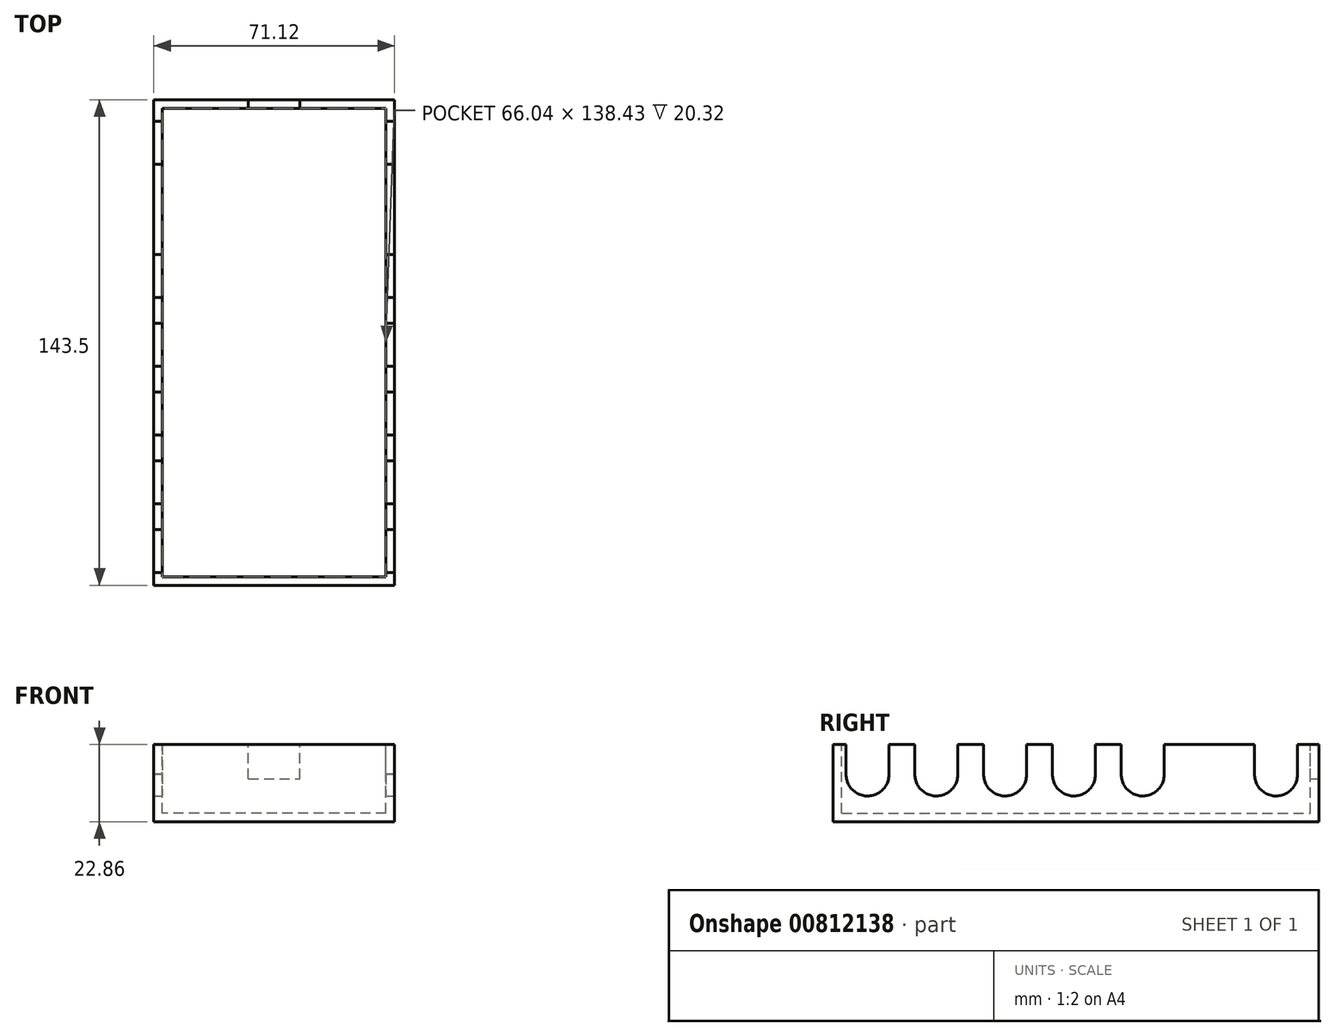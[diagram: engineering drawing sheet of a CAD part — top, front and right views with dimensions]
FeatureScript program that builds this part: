
annotation { "Feature Type Name" : "Feature", "Feature Type Description" : "" }
export const myFeature = defineFeature(function(context is Context, id is Id, definition is map)
    precondition{}
    {
        {
            var Q0;
            Q0=qCreatedBy(makeId("Top.planeOp"),FACE);
            var sketch = newSketch(context, id + "F0", { "sketchPlane" : qUnion([Q0])});
            skLineSegment(sketch, "E0.bottom", {"start": v(-35.56, -71.76) * mm, "end": v(35.56, -71.76) * mm});
            skLineSegment(sketch, "E0.top", {"start": v(-35.56, 71.76) * mm, "end": v(35.56, 71.76) * mm});
            skLineSegment(sketch, "E0.left", {"start": v(-35.56, -71.76) * mm, "end": v(-35.56, 71.76) * mm});
            skLineSegment(sketch, "E0.right", {"start": v(35.56, -71.76) * mm, "end": v(35.56, 71.76) * mm});
            skPoint(sketch, "E0.middle", {"position": v(0, 0) * mm});
            skSolve(sketch);
        }
        {
            var Q0;
            Q0 = qSketchRegion(id + "F0", true);
            extrude(context, id + "F1", {"entities" : qUnion([Q0]), "depth" : 22.86 * mm, "offsetDistance" : 25.4 * mm});
        }
        {
            var Q0;
            Q0=makeQuery(id+"F1.opExtrude","CAP_FACE",FACE,{"disambiguationData":[OSD([sQuery(id+"F0.wireOp",EDGE,"E0.bottom"),sQuery(id+"F0.wireOp",EDGE,"E0.top"),sQuery(id+"F0.wireOp",EDGE,"E0.left"),sQuery(id+"F0.wireOp",EDGE,"E0.right")])],"isStart":false});
            var sketch = newSketch(context, id + "F2", { "sketchPlane" : qUnion([Q0])});
            skLineSegment(sketch, "E1.0", {"start": v(33.02, 69.22) * mm, "end": v(-33.02, 69.22) * mm});
            skLineSegment(sketch, "E1.1", {"start": v(33.02, -69.22) * mm, "end": v(33.02, 69.22) * mm});
            skLineSegment(sketch, "E1.2", {"start": v(-33.02, -69.22) * mm, "end": v(33.02, -69.22) * mm});
            skLineSegment(sketch, "E1.3", {"start": v(-33.02, 69.22) * mm, "end": v(-33.02, -69.22) * mm});
            skSolve(sketch);
        }
        {
            var Q0;
            Q0 = qSketchRegion(id + "F2", true);
            extrude(context, id + "F3", {"entities" : qUnion([Q0]), "operationType" : NewBodyOperationType.REMOVE, "oppositeDirection" : true, "depth" : 20.32 * mm, "offsetDistance" : 25.4 * mm});
        }
        {
            var Q0;
            Q0=makeQuery(id+"F1.opExtrude","SWEPT_FACE",FACE,{"disambiguationData":[OSD([sQuery(id+"F0.wireOp",EDGE,"E0.right")])]});
            var sketch = newSketch(context, id + "F4", { "sketchPlane" : qUnion([Q0])});
            skArc(sketch, "E2", {"start": v(-67.94, 14.06) * mm, "mid": v(-61.54, 7.62) * mm, "end": v(-55.25, 14.18) * mm});
            skLineSegment(sketch, "E3", {"start": v(-67.94, 14.06) * mm, "end": v(-67.94, 22.86) * mm});
            skLineSegment(sketch, "E4", {"start": v(-55.25, 13.76) * mm, "end": v(-55.25, 22.86) * mm});
            skLineSegment(sketch, "E5", {"start": v(-55.25, 22.86) * mm, "end": v(-67.94, 22.86) * mm});
            skLineSegment(sketch, "E6.1.0.0", {"start": v(-34.93, 22.86) * mm, "end": v(-47.62, 22.86) * mm});
            skLineSegment(sketch, "E6.1.0.1", {"start": v(-34.93, 13.76) * mm, "end": v(-34.93, 22.86) * mm});
            skLineSegment(sketch, "E6.1.0.2", {"start": v(-47.62, 14.06) * mm, "end": v(-47.62, 22.86) * mm});
            skArc(sketch, "E6.1.0.3", {"start": v(-47.62, 14.06) * mm, "mid": v(-41.22, 7.62) * mm, "end": v(-34.93, 14.18) * mm});
            skLineSegment(sketch, "E6.2.0.0", {"start": v(-14.6, 22.86) * mm, "end": v(-27.3, 22.86) * mm});
            skLineSegment(sketch, "E6.2.0.1", {"start": v(-14.6, 13.76) * mm, "end": v(-14.6, 22.86) * mm});
            skLineSegment(sketch, "E6.2.0.2", {"start": v(-27.3, 14.06) * mm, "end": v(-27.3, 22.86) * mm});
            skArc(sketch, "E6.2.0.3", {"start": v(-27.3, 14.06) * mm, "mid": v(-20.9, 7.62) * mm, "end": v(-14.6, 14.18) * mm});
            skLineSegment(sketch, "E6.3.0.0", {"start": v(5.71, 22.86) * mm, "end": v(-6.98, 22.86) * mm});
            skLineSegment(sketch, "E6.3.0.1", {"start": v(5.71, 13.76) * mm, "end": v(5.71, 22.86) * mm});
            skLineSegment(sketch, "E6.3.0.2", {"start": v(-6.98, 14.06) * mm, "end": v(-6.98, 22.86) * mm});
            skArc(sketch, "E6.3.0.3", {"start": v(-6.98, 14.06) * mm, "mid": v(-0.58, 7.62) * mm, "end": v(5.71, 14.18) * mm});
            skLineSegment(sketch, "E6.4.0.0", {"start": v(26.03, 22.86) * mm, "end": v(13.34, 22.86) * mm});
            skLineSegment(sketch, "E6.4.0.1", {"start": v(26.03, 13.76) * mm, "end": v(26.03, 22.86) * mm});
            skLineSegment(sketch, "E6.4.0.2", {"start": v(13.34, 14.06) * mm, "end": v(13.34, 22.86) * mm});
            skArc(sketch, "E6.4.0.3", {"start": v(13.34, 14.06) * mm, "mid": v(19.74, 7.62) * mm, "end": v(26.03, 14.18) * mm});
            skLineSegment(sketch, "E6.direction1", {"start": v(-67.94, 14.06) * mm, "end": v(-47.62, 14.06) * mm, "construction": true});
            skArc(sketch, "E7.1.0.0", {"start": v(52.7, 14.06) * mm, "mid": v(59.11, 7.62) * mm, "end": v(65.4, 14.18) * mm});
            skLineSegment(sketch, "E7.1.0.1", {"start": v(52.7, 14.06) * mm, "end": v(52.7, 22.86) * mm});
            skLineSegment(sketch, "E7.1.0.2", {"start": v(65.4, 13.76) * mm, "end": v(65.4, 22.86) * mm});
            skLineSegment(sketch, "E7.1.0.3", {"start": v(65.4, 22.86) * mm, "end": v(52.7, 22.86) * mm});
            skLineSegment(sketch, "E7.direction1", {"start": v(-67.94, 14.06) * mm, "end": v(52.7, 14.06) * mm, "construction": true});
            skSolve(sketch);
        }
        {
            var Q0;
            Q0 = qSketchRegion(id + "F4", true);
            extrude(context, id + "F5", {"entities" : qUnion([Q0]), "operationType" : NewBodyOperationType.REMOVE, "endBound" : BoundingType.THROUGH_ALL, "oppositeDirection" : true, "depth" : 25.4 * mm, "offsetDistance" : 25.4 * mm});
        }
        {
            var Q0;
            Q0=makeQuery(id+"F1.opExtrude","SWEPT_FACE",FACE,{"disambiguationData":[OSD([sQuery(id+"F0.wireOp",EDGE,"E0.top")])]});
            var sketch = newSketch(context, id + "F6", { "sketchPlane" : qUnion([Q0])});
            skLineSegment(sketch, "E8.bottom", {"start": v(7.62, 12.7) * mm, "end": v(-7.62, 12.7) * mm});
            skLineSegment(sketch, "E8.top", {"start": v(7.62, 33.02) * mm, "end": v(-7.62, 33.02) * mm});
            skLineSegment(sketch, "E8.left", {"start": v(7.62, 12.7) * mm, "end": v(7.62, 33.02) * mm});
            skLineSegment(sketch, "E8.right", {"start": v(-7.62, 12.7) * mm, "end": v(-7.62, 33.02) * mm});
            skPoint(sketch, "E8.middle", {"position": v(0, 22.86) * mm});
            skSolve(sketch);
        }
        {
            var Q0;
            Q0 = qSketchRegion(id + "F6", true);
            extrude(context, id + "F7", {"entities" : qUnion([Q0]), "operationType" : NewBodyOperationType.REMOVE, "oppositeDirection" : true, "depth" : 25.4 * mm, "offsetDistance" : 25.4 * mm});
        }
    });
